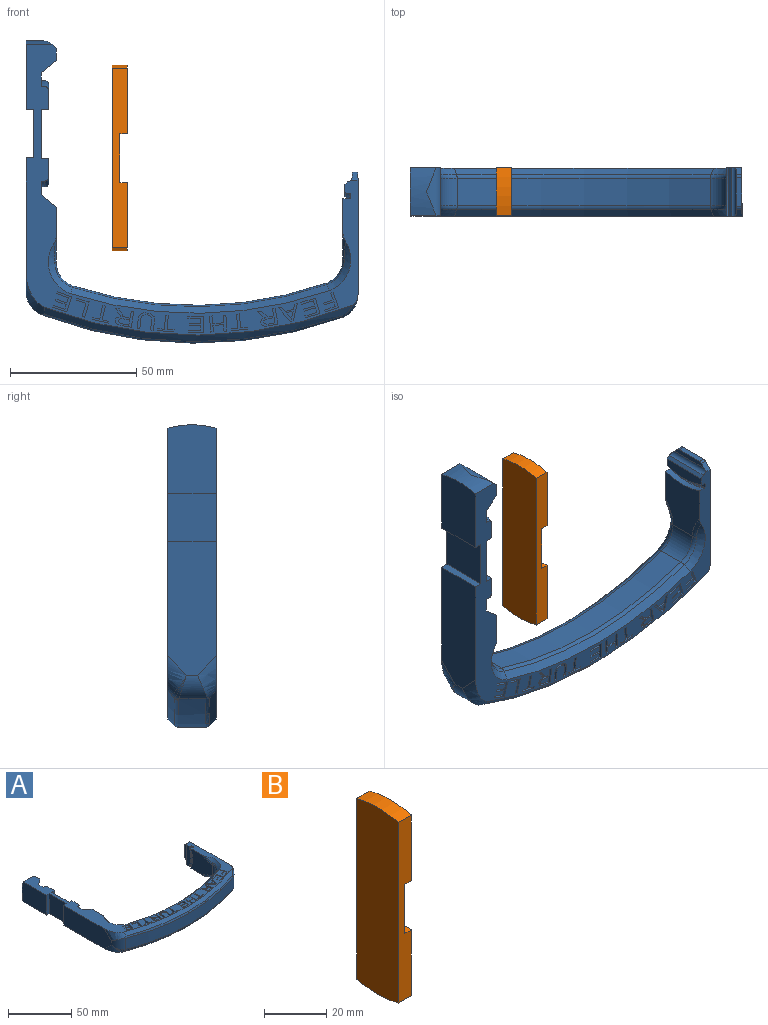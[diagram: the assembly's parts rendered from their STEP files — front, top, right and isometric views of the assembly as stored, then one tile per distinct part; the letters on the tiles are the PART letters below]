
ASSEMBLY  parts=2 mates=1
PART A: 330 faces, bbox 134.4x136.2x59.5 mm
  f0: plane 19.05x1.14mm, normal (-0.71,0.71,0), area 30.8mm2, adj f1,f5,f16,f272
  f1: plane 19.05x4.75mm, normal (-1,0,0), area 78.6mm2, adj f0,f7,f16,f272
  f2: torus R=25.78mm, axis (-1,0,0), area 11.7mm2, adj f3,f6,f16,f272
  f3: plane 19.05x3.09mm, normal (-1,0,0), area 24.8mm2, adj f2,f4,f16,f272
  f4: torus R=27.05mm, axis (-1,0,0), area 11.7mm2, adj f3,f8,f16,f272
  f5: plane 19.05x0.01mm, normal (0,1,0), area 0.1mm2, adj f0,f13,f16,f272
  f6: cylinder r=25.4mm len=19.05mm, axis (1,0,0), area 26.3mm2, adj f2,f7,f16,f272
  f7: cone r=25.15mm half-angle=45deg, axis (1,0,0), area 14mm2, adj f1,f6,f16,f272
  f8: cylinder r=27.43mm len=19.05mm, axis (1,0,0), area 51mm2, adj f4,f16,f18,f272
  f9: plane 2.81x2.81mm, normal (0,0.71,0.71), area 9mm2, adj f10,f12,f13,f16,f17
  f10: cylinder r=1.52mm len=2.29mm, axis (-1,0,0), area 2.7mm2, adj f9,f11,f12,f17
  f11: plane 11.44x2.29mm, normal (0,1,0), area 26.1mm2, adj f10,f12,f15,f17
  f12: plane 16.71x2.01mm, normal (-1,0,0), area 29.4mm2, adj f9,f10,f11,f13,f14,f15
  f13: cylinder r=1.8mm len=19.05mm, axis (0,0,1), area 52.5mm2, adj f5,f9,f12,f14,f16,f272
  f14: plane 2.81x2.81mm, normal (0,0.71,-0.71), area 9mm2, adj f12,f13,f15,f17,f272
  f15: cylinder r=1.52mm len=2.29mm, axis (1,0,0), area 2.7mm2, adj f11,f12,f14,f17
  f16: plane 133.92x117.71mm, normal (0,0,1), area 1900.7mm2, adj f0,f1,f2,f3,f4,f5,f6,f7
  f17: plane 48.39x19.05mm, normal (1,0,0), area 911.7mm2, adj f9,f10,f11,f14,f15,f16,f272,f284
  f18: plane 24.1x19.05mm, normal (-1,0,0), area 379.2mm2, adj f8,f16,f272,f277,f308,f315
  f19: plane 6.1x1.77mm, normal (-0.96,0.28,0), area 9.7mm2, adj f16,f20,f24,f25
  f20: plane 4.95x1.52mm, normal (-0.28,-0.96,0), area 7.9mm2, adj f16,f19,f21,f25
  f21: plane 1.52x0.72mm, normal (0.96,-0.28,0), area 1.1mm2, adj f16,f20,f22,f25
  f22: plane 3.9x1.52mm, normal (0.28,0.96,0), area 6.2mm2, adj f16,f21,f23,f25
  f23: plane 5.38x1.55mm, normal (0.96,-0.28,0), area 8.5mm2, adj f16,f22,f24,f25
  f24: plane 1.52x1.05mm, normal (0.28,0.96,0), area 1.7mm2, adj f16,f19,f23,f25
  f25: plane 7.53x5.16mm, normal (0,0,1), area 10mm2, adj f19,f20,f21,f22,f23,f24
  f26: plane 6.26x1.52mm, normal (-0.99,0.17,0), area 9.7mm2, adj f16,f27,f39,f73
  f27: plane 1.52x1.07mm, normal (-0.18,-0.98,0), area 1.7mm2, adj f16,f26,f28,f73
  f28: plane 2.78x1.52mm, normal (0.98,-0.17,0), area 4.3mm2, adj f16,f27,f29,f73
  f29: plane 1.52x1.25mm, normal (-0.17,-0.99,0), area 1.9mm2, adj f16,f28,f58,f73
  f30: plane 1.52x0.69mm, normal (-0.01,-1,0), area 1.1mm2, adj f16,f31,f72,f73
  f31: plane 1.52x0.64mm, normal (0.14,-0.99,0), area 1mm2, adj f16,f30,f32,f73
  f32: plane 1.52x0.5mm, normal (0.36,-0.93,0), area 0.8mm2, adj f16,f31,f52,f73
  f33: plane 2.07x1.52mm, normal (0.99,-0.17,0), area 3.2mm2, adj f34,f51,f73,f290
  f34: plane 2.57x1.52mm, normal (-0.17,-0.98,0), area 4mm2, adj f33,f40,f73,f290
  f35: plane 1.52x0.5mm, normal (0.58,0.81,0), area 0.9mm2, adj f16,f36,f57,f73
  f36: plane 1.52x0.24mm, normal (0.41,0.91,0), area 0.4mm2, adj f16,f35,f37,f73
  f37: plane 1.52x0.6mm, normal (0.29,0.96,0), area 1mm2, adj f16,f36,f38,f73
  f38: plane 1.52x0.78mm, normal (0.21,0.98,0), area 1.2mm2, adj f16,f37,f39,f73
  f39: plane 3.61x1.52mm, normal (0.17,0.98,0), area 5.6mm2, adj f16,f26,f38,f73
  f40: plane 1.52x0.12mm, normal (-0.14,-0.99,0), area 0.2mm2, adj f34,f41,f73,f290
  f41: plane 1.52x0.69mm, normal (-0.29,-0.96,0), area 1.1mm2, adj f40,f42,f73,f290
  f42: plane 1.52x0.47mm, normal (-0.53,-0.85,0), area 0.8mm2, adj f41,f43,f73,f290
  f43: plane 1.52x0.28mm, normal (-0.79,-0.61,0), area 0.5mm2, adj f42,f44,f73,f290
  f44: plane 1.52x0.52mm, normal (-0.99,-0.13,0), area 0.8mm2, adj f43,f45,f73,f290
  f45: plane 1.52x0.08mm, normal (-0.98,0.22,0), area 0.1mm2, adj f44,f46,f73,f290
  f46: plane 1.52x0.44mm, normal (-0.83,0.55,0), area 0.8mm2, adj f45,f47,f73,f290
  f47: plane 1.52x0.11mm, normal (-0.57,0.82,0), area 0.2mm2, adj f46,f48,f73,f290
  f48: plane 1.52x0.59mm, normal (-0.3,0.96,0), area 0.9mm2, adj f47,f49,f73,f290
  f49: plane 1.52x0.43mm, normal (-0.02,1,0), area 0.7mm2, adj f48,f50,f73,f290
  f50: plane 1.52x0.74mm, normal (0.11,0.99,0), area 1.1mm2, adj f49,f51,f73,f290
  f51: plane 2.31x1.52mm, normal (0.17,0.98,0), area 3.6mm2, adj f33,f50,f73,f290
  f52: plane 1.52x0.22mm, normal (0.52,-0.85,0), area 0.4mm2, adj f16,f32,f53,f73
  f53: plane 1.52x0.39mm, normal (0.74,-0.68,0), area 0.8mm2, adj f16,f52,f54,f73
  f54: plane 1.52x0.49mm, normal (0.94,-0.35,0), area 0.8mm2, adj f16,f53,f55,f73
  f55: plane 1.52x0.49mm, normal (1,0,0), area 0.8mm2, adj f16,f54,f56,f73
  f56: plane 1.52x0.51mm, normal (0.95,0.33,0), area 0.8mm2, adj f16,f55,f57,f73
  f57: plane 1.52x0.39mm, normal (0.8,0.6,0), area 0.7mm2, adj f16,f35,f56,f73
  f58: plane 1.52x0.59mm, normal (-0.22,-0.98,0), area 0.9mm2, adj f16,f29,f59,f73
  f59: plane 1.52x0.46mm, normal (-0.48,-0.88,0), area 0.8mm2, adj f16,f58,f60,f73
  f60: plane 1.52x0.06mm, normal (-0.65,-0.76,0), area 0.1mm2, adj f16,f59,f61,f73
  f61: plane 1.52x0.47mm, normal (-0.75,-0.66,0), area 0.9mm2, adj f16,f60,f62,f73
  f62: plane 1.52x0.01mm, normal (-0.71,-0.71,0), area 0mm2, adj f16,f61,f63,f73
  f63: plane 1.52x0.42mm, normal (-0.83,-0.55,0), area 0.8mm2, adj f16,f62,f64,f73
  f64: plane 1.52x0.57mm, normal (-0.86,-0.52,0), area 1mm2, adj f16,f63,f65,f73
  f65: plane 1.52x1.49mm, normal (-0.87,-0.49,0), area 2.6mm2, adj f16,f64,f66,f73
  f66: plane 1.52x1.36mm, normal (-0.17,-0.99,0), area 2.1mm2, adj f16,f65,f67,f73
  f67: plane 1.95x1.52mm, normal (0.87,0.5,0), area 3.4mm2, adj f16,f66,f68,f73
  f68: plane 1.52x0.05mm, normal (0.83,0.55,0), area 0.1mm2, adj f16,f67,f69,f73
  f69: plane 1.52x0.5mm, normal (0.83,0.56,0), area 0.9mm2, adj f16,f68,f70,f73
  f70: plane 1.52x0.44mm, normal (0.76,0.65,0), area 0.9mm2, adj f16,f69,f71,f73
  f71: plane 1.52x0.05mm, normal (0.71,0.71,0), area 0.1mm2, adj f16,f70,f72,f73
  f72: plane 1.52x0.54mm, normal (0.57,0.82,0), area 1mm2, adj f16,f30,f71,f73
  f73: plane 7.51x7.29mm, normal (0,0,1), area 19.9mm2, adj f26,f27,f28,f29,f30,f31,f32,f33
  f74: plane 3.65x1.52mm, normal (-0.99,0.12,0), area 5.6mm2, adj f16,f75,f89,f113
  f75: plane 1.52x0.06mm, normal (-0.99,0.14,0), area 0.1mm2, adj f16,f74,f76,f113
  f76: plane 1.52x0.6mm, normal (-1,0.06,0), area 0.9mm2, adj f16,f75,f77,f113
  f77: plane 1.52x0.52mm, normal (-1,-0.1,0), area 0.8mm2, adj f16,f76,f78,f113
  f78: plane 1.52x0.44mm, normal (-0.97,-0.26,0), area 0.7mm2, adj f16,f77,f79,f113
  f79: plane 1.52x0.19mm, normal (-0.92,-0.4,0), area 0.3mm2, adj f16,f78,f80,f113
  f80: plane 1.52x0.45mm, normal (-0.79,-0.61,0), area 0.9mm2, adj f16,f79,f98,f113
  f81: plane 1.52x0.59mm, normal (0.18,0.98,0), area 0.9mm2, adj f16,f82,f97,f113
  f82: plane 1.52x0.57mm, normal (0.39,0.92,0), area 0.9mm2, adj f16,f81,f83,f113
  f83: plane 1.52x0.3mm, normal (0.59,0.81,0), area 0.6mm2, adj f16,f82,f84,f113
  f84: plane 1.52x0.47mm, normal (0.83,0.55,0), area 0.9mm2, adj f16,f83,f85,f113
  f85: plane 1.52x0.13mm, normal (0.95,0.3,0), area 0.2mm2, adj f16,f84,f86,f113
  f86: plane 1.52x0.48mm, normal (0.99,0.1,0), area 0.7mm2, adj f16,f85,f87,f113
  f87: plane 1.52x0.62mm, normal (1,-0.07,0), area 0.9mm2, adj f16,f86,f88,f113
  f88: plane 3.64x1.52mm, normal (0.99,-0.12,0), area 5.6mm2, adj f16,f87,f89,f113
  f89: plane 1.52x1.09mm, normal (0.12,0.99,0), area 1.7mm2, adj f16,f74,f88,f113
  f90: plane 3.64x1.52mm, normal (-0.99,0.12,0), area 5.6mm2, adj f16,f91,f112,f113
  f91: plane 1.52x0.21mm, normal (-0.99,0.16,0), area 0.3mm2, adj f16,f90,f92,f113
  f92: plane 1.52x0.59mm, normal (-0.97,0.25,0), area 0.9mm2, adj f16,f91,f93,f113
  f93: plane 1.52x0.44mm, normal (-0.9,0.44,0), area 0.8mm2, adj f16,f92,f94,f113
  f94: plane 1.52x0.3mm, normal (-0.7,0.72,0), area 0.6mm2, adj f16,f93,f95,f113
  f95: plane 1.52x0.37mm, normal (-0.4,0.92,0), area 0.6mm2, adj f16,f94,f96,f113
  f96: plane 1.52x0.61mm, normal (-0.15,0.99,0), area 0.9mm2, adj f16,f95,f97,f113
  f97: plane 1.52x0.78mm, normal (0.05,1,0), area 1.2mm2, adj f16,f81,f96,f113
  f98: plane 1.52x0.5mm, normal (-0.59,-0.81,0), area 0.9mm2, adj f16,f80,f99,f113
  f99: plane 1.52x0.47mm, normal (-0.42,-0.91,0), area 0.8mm2, adj f16,f98,f100,f113
  f100: plane 1.52x0.64mm, normal (-0.29,-0.96,0), area 1mm2, adj f16,f99,f101,f113
  f101: plane 1.52x0.74mm, normal (-0.17,-0.99,0), area 1.1mm2, adj f16,f100,f102,f113
  f102: plane 1.52x0.74mm, normal (-0.07,-1,0), area 1.1mm2, adj f16,f101,f103,f113
  f103: plane 1.52x0.66mm, normal (0.06,-1,0), area 1mm2, adj f16,f102,f104,f113
  f104: plane 1.52x0.57mm, normal (0.23,-0.97,0), area 0.9mm2, adj f16,f103,f105,f113
  f105: plane 1.52x0.23mm, normal (0.35,-0.94,0), area 0.4mm2, adj f16,f104,f106,f113
  f106: plane 1.52x0.52mm, normal (0.5,-0.86,0), area 0.9mm2, adj f16,f105,f107,f113
  f107: plane 1.52x0.4mm, normal (0.74,-0.68,0), area 0.8mm2, adj f16,f106,f108,f113
  f108: plane 1.52x0.38mm, normal (0.88,-0.47,0), area 0.7mm2, adj f16,f107,f109,f113
  f109: plane 1.52x0.5mm, normal (0.95,-0.3,0), area 0.8mm2, adj f16,f108,f110,f113
  f110: plane 1.52x0.59mm, normal (0.99,-0.17,0), area 0.9mm2, adj f16,f109,f111,f113
  f111: plane 3.64x1.52mm, normal (0.99,-0.12,0), area 5.6mm2, adj f16,f110,f112,f113
  f112: plane 1.52x1.09mm, normal (0.12,0.99,0), area 1.7mm2, adj f16,f90,f111,f113
  f113: plane 6.93x6.86mm, normal (0,0,1), area 15.8mm2, adj f74,f75,f76,f77,f78,f79,f80,f81
  f114: plane 6.35x1.52mm, normal (-1,0,0), area 9.7mm2, adj f16,f115,f125,f126
  f115: plane 6.16x1.52mm, normal (0,-1,0), area 9.4mm2, adj f16,f114,f116,f126
  f116: plane 1.52x0.75mm, normal (1,0,0), area 1.1mm2, adj f16,f115,f117,f126
  f117: plane 5.06x1.52mm, normal (0,1,0), area 7.7mm2, adj f16,f116,f118,f126
  f118: plane 2.17x1.52mm, normal (1,0,0), area 3.3mm2, adj f16,f117,f119,f126
  f119: plane 4.56x1.52mm, normal (0,-1,0), area 6.9mm2, adj f16,f118,f120,f126
  f120: plane 1.52x0.74mm, normal (1,0,0), area 1.1mm2, adj f16,f119,f121,f126
  f121: plane 4.56x1.52mm, normal (0,1,0), area 6.9mm2, adj f16,f120,f122,f126
  f122: plane 1.94x1.52mm, normal (1,0,0), area 3mm2, adj f16,f121,f123,f126
  f123: plane 4.87x1.52mm, normal (0,-1,0), area 7.4mm2, adj f16,f122,f124,f126
  f124: plane 1.52x0.74mm, normal (1,0,0), area 1.1mm2, adj f16,f123,f125,f126
  f125: plane 5.96x1.52mm, normal (0,1,0), area 9.1mm2, adj f16,f114,f124,f126
  f126: plane 6.35x6.16mm, normal (0,0,1), area 17.8mm2, adj f114,f115,f116,f117,f118,f119,f120,f121
  f127: plane 6.34x1.52mm, normal (-1,-0.06,0), area 9.7mm2, adj f16,f128,f132,f139
  f128: plane 1.52x1.09mm, normal (0.05,-1,0), area 1.7mm2, adj f16,f127,f129,f139
  f129: plane 2.99x1.52mm, normal (1,0.06,0), area 4.6mm2, adj f16,f128,f130,f139
  f130: plane 4.28x1.52mm, normal (0.05,-1,0), area 6.5mm2, adj f16,f129,f135,f139
  f131: plane 2.61x1.52mm, normal (1,0.05,0), area 4mm2, adj f16,f132,f134,f139
  f132: plane 1.52x1.1mm, normal (-0.05,1,0), area 1.7mm2, adj f16,f127,f131,f139
  f133: plane 2.61x1.52mm, normal (-1,-0.05,0), area 4mm2, adj f16,f134,f138,f139
  f134: plane 4.27x1.52mm, normal (-0.05,1,0), area 6.5mm2, adj f16,f131,f133,f139
  f135: plane 2.99x1.52mm, normal (-1,-0.06,0), area 4.6mm2, adj f16,f130,f136,f139
  f136: plane 1.52x1.09mm, normal (0.05,-1,0), area 1.7mm2, adj f16,f135,f137,f139
  f137: plane 6.34x1.52mm, normal (1,0.05,0), area 9.7mm2, adj f16,f136,f138,f139
  f138: plane 1.52x1.09mm, normal (-0.05,1,0), area 1.7mm2, adj f16,f133,f137,f139
  f139: plane 6.81x6.69mm, normal (0,0,1), area 17.1mm2, adj f127,f128,f129,f130,f131,f132,f133,f134
  f140: plane 6.25x1.52mm, normal (-0.98,-0.18,0), area 9.7mm2, adj f16,f141,f153,f187
  f141: plane 1.52x1.08mm, normal (0.18,-0.98,0), area 1.7mm2, adj f16,f140,f142,f187
  f142: plane 2.78x1.52mm, normal (0.98,0.18,0), area 4.3mm2, adj f16,f141,f143,f187
  f143: plane 1.52x1.25mm, normal (0.18,-0.98,0), area 1.9mm2, adj f16,f142,f172,f187
  f144: plane 1.52x0.65mm, normal (0.34,-0.94,0), area 1.1mm2, adj f16,f145,f186,f187
  f145: plane 1.52x0.57mm, normal (0.47,-0.88,0), area 1mm2, adj f16,f144,f146,f187
  f146: plane 1.52x0.4mm, normal (0.66,-0.75,0), area 0.8mm2, adj f16,f145,f166,f187
  f147: plane 2.07x1.52mm, normal (0.98,0.18,0), area 3.2mm2, adj f148,f165,f187,f271
  f148: plane 2.57x1.52mm, normal (0.18,-0.98,0), area 4mm2, adj f147,f154,f187,f271
  f149: plane 1.52x0.59mm, normal (0.27,0.96,0), area 0.9mm2, adj f16,f150,f171,f187
  f150: plane 1.52x0.26mm, normal (0.06,1,0), area 0.4mm2, adj f16,f149,f151,f187
  f151: plane 1.52x0.64mm, normal (-0.05,1,0), area 1mm2, adj f16,f150,f152,f187
  f152: plane 1.52x0.79mm, normal (-0.15,0.99,0), area 1.2mm2, adj f16,f151,f153,f187
  f153: plane 3.6x1.52mm, normal (-0.18,0.98,0), area 5.6mm2, adj f16,f140,f152,f187
  f154: plane 1.52x0.11mm, normal (0.15,-0.99,0), area 0.2mm2, adj f148,f155,f187,f271
  f155: plane 1.52x0.73mm, normal (0.07,-1,0), area 1.1mm2, adj f154,f156,f187,f271
  f156: plane 1.52x0.54mm, normal (-0.21,-0.98,0), area 0.8mm2, adj f155,f157,f187,f271
  f157: plane 1.52x0.31mm, normal (-0.54,-0.84,0), area 0.6mm2, adj f156,f158,f187,f271
  f158: plane 1.52x0.45mm, normal (-0.88,-0.47,0), area 0.8mm2, adj f157,f159,f187,f271
  f159: plane 1.52x0.08mm, normal (-1,-0.1,0), area 0.1mm2, adj f158,f160,f187,f271
  f160: plane 1.52x0.52mm, normal (-0.97,0.24,0), area 0.8mm2, adj f159,f161,f187,f271
  f161: plane 1.52x0.11mm, normal (-0.82,0.57,0), area 0.2mm2, adj f160,f162,f187,f271
  f162: plane 1.52x0.49mm, normal (-0.61,0.8,0), area 0.9mm2, adj f161,f163,f187,f271
  f163: plane 1.52x0.39mm, normal (-0.36,0.93,0), area 0.6mm2, adj f162,f164,f187,f271
  f164: plane 1.52x0.74mm, normal (-0.23,0.97,0), area 1.2mm2, adj f163,f165,f187,f271
  f165: plane 2.31x1.52mm, normal (-0.17,0.98,0), area 3.6mm2, adj f147,f164,f187,f271
  f166: plane 1.52x0.21mm, normal (0.81,-0.58,0), area 0.4mm2, adj f16,f146,f167,f187
  f167: plane 1.52x0.49mm, normal (0.92,-0.4,0), area 0.8mm2, adj f16,f166,f168,f187
  f168: plane 1.52x0.53mm, normal (1,0,0), area 0.8mm2, adj f16,f167,f169,f187
  f169: plane 1.52x0.47mm, normal (0.94,0.34,0), area 0.8mm2, adj f16,f168,f170,f187
  f170: plane 1.52x0.42mm, normal (0.78,0.62,0), area 0.8mm2, adj f16,f169,f171,f187
  f171: plane 1.52x0.42mm, normal (0.54,0.84,0), area 0.8mm2, adj f16,f149,f170,f187
  f172: plane 1.52x0.61mm, normal (0.12,-0.99,0), area 0.9mm2, adj f16,f143,f173,f187
  f173: plane 1.52x0.52mm, normal (-0.14,-0.99,0), area 0.8mm2, adj f16,f172,f174,f187
  f174: plane 1.52x0.07mm, normal (-0.35,-0.94,0), area 0.1mm2, adj f16,f173,f175,f187
  f175: plane 1.52x0.55mm, normal (-0.48,-0.88,0), area 1mm2, adj f16,f174,f176,f187
  f176: plane 1.52x0.01mm, normal (0,-1,0), area 0mm2, adj f16,f175,f177,f187
  f177: plane 1.52x0.41mm, normal (-0.59,-0.81,0), area 0.8mm2, adj f16,f176,f178,f187
  f178: plane 1.52x0.51mm, normal (-0.63,-0.77,0), area 1mm2, adj f16,f177,f179,f187
  f179: plane 1.52x1.31mm, normal (-0.65,-0.76,0), area 2.6mm2, adj f16,f178,f180,f187
  f180: plane 1.52x1.36mm, normal (0.18,-0.98,0), area 2.1mm2, adj f16,f179,f181,f187
  f181: plane 1.72x1.52mm, normal (0.65,0.76,0), area 3.4mm2, adj f16,f180,f182,f187
  f182: plane 1.52x0.05mm, normal (0.55,0.83,0), area 0.1mm2, adj f16,f181,f183,f187
  f183: plane 1.52x0.49mm, normal (0.59,0.81,0), area 0.9mm2, adj f16,f182,f184,f187
  f184: plane 1.52x0.5mm, normal (0.48,0.88,0), area 0.9mm2, adj f16,f183,f185,f187
  f185: plane 1.52x0.07mm, normal (0.35,0.94,0), area 0.1mm2, adj f16,f184,f186,f187
  f186: plane 1.52x0.64mm, normal (0.25,0.97,0), area 1mm2, adj f16,f144,f185,f187
  f187: plane 8.27x7.04mm, normal (0,0,1), area 19.9mm2, adj f140,f141,f142,f143,f144,f145,f146,f147
  f188: plane 1.52x0.24mm, normal (-0.82,-0.57,0), area 0.4mm2, adj f189,f203,f205,f270
  f189: plane 1.52x0.42mm, normal (-0.8,-0.61,0), area 0.8mm2, adj f188,f190,f205,f270
  f190: plane 1.52x0.49mm, normal (-0.79,-0.61,0), area 1mm2, adj f189,f191,f205,f270
  f191: plane 1.52x1.51mm, normal (-0.77,-0.63,0), area 3mm2, adj f190,f192,f205,f270
  f192: plane 2.72x1.52mm, normal (-0.23,0.97,0), area 4.3mm2, adj f191,f200,f205,f270
  f193: plane 1.65x1.52mm, normal (-0.77,-0.64,0), area 3.3mm2, adj f16,f194,f199,f205
  f194: plane 1.52x1.2mm, normal (0.23,-0.97,0), area 1.9mm2, adj f16,f193,f195,f205
  f195: plane 5.41x4.73mm, normal (0.75,0.66,0), area 11mm2, adj f16,f194,f204,f205
  f196: plane 6.91x1.64mm, normal (-0.97,0.23,0), area 10.8mm2, adj f16,f197,f204,f205
  f197: plane 1.52x1.13mm, normal (0.23,-0.97,0), area 1.8mm2, adj f16,f196,f198,f205
  f198: plane 2.08x1.52mm, normal (0.98,-0.21,0), area 3.2mm2, adj f16,f197,f199,f205
  f199: plane 3.35x1.52mm, normal (0.23,-0.97,0), area 5.2mm2, adj f16,f193,f198,f205
  f200: plane 2.02x1.52mm, normal (0.97,-0.22,0), area 3.2mm2, adj f192,f201,f205,f270
  f201: plane 1.52x0.22mm, normal (0.98,-0.19,0), area 0.3mm2, adj f200,f202,f205,f270
  f202: plane 1.52x0.54mm, normal (0.99,-0.14,0), area 0.8mm2, adj f201,f203,f205,f270
  f203: plane 1.52x0.54mm, normal (1,-0.06,0), area 0.8mm2, adj f188,f202,f205,f270
  f204: plane 1.52x1.15mm, normal (-0.23,0.97,0), area 1.8mm2, adj f16,f195,f196,f205
  f205: plane 7.51x7.18mm, normal (0,0,1), area 15.7mm2, adj f188,f189,f190,f191,f192,f193,f194,f195
  f206: plane 6.01x2.06mm, normal (-0.95,-0.32,0), area 9.7mm2, adj f16,f207,f215,f216
  f207: plane 1.52x1.04mm, normal (0.33,-0.94,0), area 1.7mm2, adj f16,f206,f208,f216
  f208: plane 2.73x1.52mm, normal (0.95,0.32,0), area 4.4mm2, adj f16,f207,f209,f216
  f209: plane 3.66x1.52mm, normal (0.32,-0.95,0), area 5.9mm2, adj f16,f208,f210,f216
  f210: plane 1.52x0.71mm, normal (0.95,0.32,0), area 1.1mm2, adj f16,f209,f211,f216
  f211: plane 3.66x1.52mm, normal (-0.32,0.95,0), area 5.9mm2, adj f16,f210,f212,f216
  f212: plane 1.86x1.52mm, normal (0.95,0.32,0), area 3mm2, adj f16,f211,f213,f216
  f213: plane 4.23x1.52mm, normal (0.33,-0.95,0), area 6.8mm2, adj f16,f212,f214,f216
  f214: plane 1.52x0.7mm, normal (0.95,0.33,0), area 1.1mm2, adj f16,f213,f215,f216
  f215: plane 5.27x1.81mm, normal (-0.32,0.95,0), area 8.5mm2, adj f16,f206,f214,f216
  f216: plane 7.81x5.82mm, normal (0,0,1), area 13.2mm2, adj f206,f207,f208,f209,f210,f211,f212,f213
  f217: plane 6.1x1.77mm, normal (-0.96,-0.28,0), area 9.7mm2, adj f16,f218,f228,f229
  f218: plane 5.91x1.72mm, normal (0.28,-0.96,0), area 9.4mm2, adj f16,f217,f219,f229
  f219: plane 1.52x0.72mm, normal (0.96,0.28,0), area 1.1mm2, adj f16,f218,f220,f229
  f220: plane 4.86x1.52mm, normal (-0.28,0.96,0), area 7.7mm2, adj f16,f219,f221,f229
  f221: plane 2.07x1.52mm, normal (0.96,0.28,0), area 3.3mm2, adj f16,f220,f222,f229
  f222: plane 4.38x1.52mm, normal (0.28,-0.96,0), area 7mm2, adj f16,f221,f223,f229
  f223: plane 1.52x0.71mm, normal (0.96,0.28,0), area 1.1mm2, adj f16,f222,f224,f229
  f224: plane 4.38x1.52mm, normal (-0.28,0.96,0), area 7mm2, adj f16,f223,f225,f229
  f225: plane 1.87x1.52mm, normal (0.96,0.27,0), area 3mm2, adj f16,f224,f226,f229
  f226: plane 4.68x1.52mm, normal (0.28,-0.96,0), area 7.4mm2, adj f16,f225,f227,f229
  f227: plane 1.52x0.72mm, normal (0.96,0.28,0), area 1.1mm2, adj f16,f226,f228,f229
  f228: plane 5.73x1.66mm, normal (-0.28,0.96,0), area 9.1mm2, adj f16,f217,f227,f229
  f229: plane 7.76x7.68mm, normal (0,0,1), area 17.8mm2, adj f217,f218,f219,f220,f221,f222,f223,f224
  f230: plane 1.52x0.75mm, normal (-1,-0.1,0), area 1.2mm2, adj f16,f231,f237,f238
  f231: plane 2.7x1.52mm, normal (0.1,-0.99,0), area 4.1mm2, adj f16,f230,f232,f238
  f232: plane 5.57x1.52mm, normal (-0.99,-0.1,0), area 8.5mm2, adj f16,f231,f233,f238
  f233: plane 1.52x1.09mm, normal (0.11,-0.99,0), area 1.7mm2, adj f16,f232,f234,f238
  f234: plane 5.57x1.52mm, normal (0.99,0.1,0), area 8.5mm2, adj f16,f233,f235,f238
  f235: plane 2.72x1.52mm, normal (0.1,-0.99,0), area 4.2mm2, adj f16,f234,f236,f238
  f236: plane 1.52x0.74mm, normal (0.99,0.11,0), area 1.1mm2, adj f16,f235,f237,f238
  f237: plane 6.5x1.52mm, normal (-0.1,0.99,0), area 10mm2, adj f16,f230,f236,f238
  f238: plane 6.72x6.58mm, normal (0,0,1), area 11mm2, adj f230,f231,f232,f233,f234,f235,f236,f237
  f239: plane 1.52x0.74mm, normal (-1,0.07,0), area 1.1mm2, adj f16,f240,f246,f247
  f240: plane 2.71x1.52mm, normal (-0.07,-1,0), area 4.1mm2, adj f16,f239,f241,f247
  f241: plane 5.58x1.52mm, normal (-1,0.07,0), area 8.5mm2, adj f16,f240,f242,f247
  f242: plane 1.52x1.09mm, normal (-0.08,-1,0), area 1.7mm2, adj f16,f241,f243,f247
  f243: plane 5.59x1.52mm, normal (1,-0.07,0), area 8.5mm2, adj f16,f242,f244,f247
  f244: plane 2.72x1.52mm, normal (-0.07,-1,0), area 4.2mm2, adj f16,f243,f245,f247
  f245: plane 1.52x0.74mm, normal (1,-0.08,0), area 1.1mm2, adj f16,f244,f246,f247
  f246: plane 6.53x1.52mm, normal (0.07,1,0), area 10mm2, adj f16,f239,f245,f247
  f247: plane 6.61x6.58mm, normal (0,0,1), area 11mm2, adj f239,f240,f241,f242,f243,f244,f245,f246
  f248: plane 1.52x0.73mm, normal (-0.97,0.23,0), area 1.1mm2, adj f16,f249,f255,f256
  f249: plane 2.65x1.52mm, normal (-0.23,-0.97,0), area 4.1mm2, adj f16,f248,f250,f256
  f250: plane 5.45x1.52mm, normal (-0.97,0.23,0), area 8.5mm2, adj f16,f249,f251,f256
  f251: plane 1.52x1.06mm, normal (-0.23,-0.97,0), area 1.7mm2, adj f16,f250,f252,f256
  f252: plane 5.45x1.52mm, normal (0.97,-0.23,0), area 8.5mm2, adj f16,f251,f253,f256
  f253: plane 2.66x1.52mm, normal (-0.22,-0.97,0), area 4.2mm2, adj f16,f252,f254,f256
  f254: plane 1.52x0.73mm, normal (0.97,-0.22,0), area 1.1mm2, adj f16,f253,f255,f256
  f255: plane 6.37x1.52mm, normal (0.23,0.97,0), area 10mm2, adj f16,f248,f254,f256
  f256: plane 7.05x6.54mm, normal (0,0,1), area 11mm2, adj f248,f249,f250,f251,f252,f253,f254,f255
  f257: plane 6.01x2.05mm, normal (-0.95,0.32,0), area 9.7mm2, adj f16,f258,f268,f269
  f258: plane 5.82x1.99mm, normal (-0.32,-0.95,0), area 9.4mm2, adj f16,f257,f259,f269
  f259: plane 1.52x0.71mm, normal (0.95,-0.32,0), area 1.1mm2, adj f16,f258,f260,f269
  f260: plane 4.79x1.64mm, normal (0.32,0.95,0), area 7.7mm2, adj f16,f259,f261,f269
  f261: plane 2.04x1.52mm, normal (0.95,-0.33,0), area 3.3mm2, adj f16,f260,f262,f269
  f262: plane 4.32x1.52mm, normal (-0.32,-0.95,0), area 7mm2, adj f16,f261,f263,f269
  f263: plane 1.52x0.7mm, normal (0.95,-0.33,0), area 1.1mm2, adj f16,f262,f264,f269
  f264: plane 4.32x1.52mm, normal (0.32,0.95,0), area 7mm2, adj f16,f263,f265,f269
  f265: plane 1.84x1.52mm, normal (0.95,-0.32,0), area 3mm2, adj f16,f264,f266,f269
  f266: plane 4.61x1.58mm, normal (-0.32,-0.95,0), area 7.4mm2, adj f16,f265,f267,f269
  f267: plane 1.52x0.71mm, normal (0.95,-0.32,0), area 1.1mm2, adj f16,f266,f268,f269
  f268: plane 5.65x1.93mm, normal (0.32,0.95,0), area 9.1mm2, adj f16,f257,f267,f269
  f269: plane 8.01x7.7mm, normal (0,0,1), area 17.8mm2, adj f257,f258,f259,f260,f261,f262,f263,f264
  f270: plane 3.3x2.72mm, normal (0,0,1), area 4.1mm2, adj f188,f189,f190,f191,f192,f200,f201,f202
  f271: plane 4.5x2.59mm, normal (0,0,1), area 8.4mm2, adj f147,f148,f154,f155,f156,f157,f158,f159
  f272: plane 132.03x115.82mm, normal (0,0,-1), area 2119.6mm2, adj f0,f1,f2,f3,f4,f5,f6,f7
  f273: torus R=12.29mm, axis (0,0,1), area 22.2mm2, adj f274,f277,f279,f315
  f274: torus R=159.79mm, axis (0,0,1), area 184mm2, adj f273,f275,f278,f316
  f275: torus R=12.29mm, axis (0,0,1), area 22.6mm2, adj f274,f276,f280,f317
  f276: bspline ~10.88x5.74mm, area 19.3mm2, adj f272,f275,f280,f318
  f277: bspline ~10.88x5.74mm, area 19.2mm2, adj f18,f272,f273,f279
  f278: cone r=159.09mm half-angle=45deg, axis (0,0,-1), area 367.2mm2, adj f272,f274,f279,f280
  f279: cone r=11.59mm half-angle=45deg, axis (0,0,-1), area 64mm2, adj f272,f273,f277,f278
  f280: cone r=11.59mm half-angle=45deg, axis (0,0,-1), area 64.9mm2, adj f272,f275,f276,f278
  f281: torus R=168.99mm, axis (0,0,-1), area 215.2mm2, adj f282,f283,f285,f326
  f282: bspline ~8.14x6.6mm, area 19.7mm2, adj f272,f281,f283,f284
  f283: cone r=169.69mm half-angle=45deg, axis (0,0,1), area 432.3mm2, adj f272,f281,f282,f328,f329
  f284: cylinder r=10mm len=19.05mm, axis (0,0,1), area 171.3mm2, adj f16,f17,f272,f282,f285,f313
  f285: cylinder r=171.28mm len=118.83mm, axis (0,0,1), area 1311.3mm2, adj f281,f284,f312,f324,f326
  f286: plane 19.05x19.05mm, normal (-1,0,0), area 362.9mm2, adj f16,f272,f319,f321
  f287: cylinder r=36.87mm len=19.05mm, axis (-1,0,0), area 161.7mm2, adj f16,f272,f288,f322
  f288: cylinder r=6.35mm len=19.05mm, axis (0,0,-1), area 88.1mm2, adj f16,f272,f287,f289
  f289: plane 19.05x4.52mm, normal (1,0,0), area 66.7mm2, adj f16,f272,f288,f299
  f290: plane 4.49x2.56mm, normal (0,0,1), area 8.4mm2, adj f33,f34,f40,f41,f42,f43,f44,f45
  f291: plane 19.05x3.02mm, normal (0,-1,0), area 57.6mm2, adj f16,f272,f293,f303
  f292: plane 19.05x3.02mm, normal (0,1,0), area 57.6mm2, adj f16,f272,f293,f294
  f293: plane 19.56x19.05mm, normal (1,0,0), area 372.6mm2, adj f16,f272,f291,f292
  f294: plane 19.05x9.7mm, normal (1,0,0), area 169.4mm2, adj f16,f272,f292,f298
  f295: cone r=28.37mm half-angle=37.8deg, axis (1,0,0), area 148.3mm2, adj f16,f272,f296,f318
  f296: plane 19.05x7.33mm, normal (1,0,0), area 98.9mm2, adj f16,f272,f295,f297
  f297: cylinder r=21mm len=19.05mm, axis (-1,0,0), area 29.2mm2, adj f16,f272,f296,f298
  f298: torus R=19.48mm, axis (1,0,0), area 48mm2, adj f16,f272,f294,f297
  f299: cone r=28.37mm half-angle=37.8deg, axis (1,0,0), area 148.3mm2, adj f16,f272,f289,f300
  f300: plane 19.05x7.33mm, normal (1,0,0), area 98.9mm2, adj f16,f272,f299,f301
  f301: cylinder r=21mm len=19.05mm, axis (1,0,0), area 29.2mm2, adj f16,f272,f300,f302
  f302: torus R=19.48mm, axis (1,0,0), area 48mm2, adj f16,f272,f301,f303
  f303: plane 19.05x9.7mm, normal (1,0,0), area 169.4mm2, adj f16,f272,f291,f302
  f304: torus R=12.29mm, axis (0,0,-1), area 22.2mm2, adj f305,f308,f310,f315
  f305: torus R=159.79mm, axis (0,0,-1), area 184mm2, adj f304,f306,f309,f316
  f306: torus R=12.29mm, axis (0,0,-1), area 22.6mm2, adj f305,f307,f311,f317
  f307: bspline ~10.88x5.74mm, area 19.3mm2, adj f16,f306,f311,f318
  f308: bspline ~10.88x5.74mm, area 19.2mm2, adj f16,f18,f304,f310
  f309: cone r=159.09mm half-angle=45deg, axis (0,0,1), area 367.2mm2, adj f16,f305,f310,f311
  f310: cone r=11.59mm half-angle=45deg, axis (0,0,1), area 63.9mm2, adj f16,f304,f308,f309
  f311: cone r=11.59mm half-angle=45deg, axis (0,0,1), area 65.1mm2, adj f16,f306,f307,f309
  f312: torus R=168.99mm, axis (0,0,1), area 218.3mm2, adj f285,f313,f314,f323,f324
  f313: bspline ~8.14x6.6mm, area 19.7mm2, adj f16,f284,f312,f314
  f314: cone r=169.69mm half-angle=45deg, axis (0,0,-1), area 433.7mm2, adj f16,f312,f313,f323
  f315: cylinder r=10mm len=10.81mm, axis (0,0,1), area 130.4mm2, adj f18,f273,f304,f316
  f316: cylinder r=157.51mm len=100.55mm, axis (0,0,1), area 1106mm2, adj f274,f305,f315,f317
  f317: cylinder r=10mm len=10.81mm, axis (0,0,1), area 133.2mm2, adj f275,f306,f316,f318
  f318: plane 21.74x19.05mm, normal (1,0,0), area 336.8mm2, adj f16,f272,f276,f295,f307,f317
  f319: plane 19.05x3mm, normal (0,1,0), area 57.1mm2, adj f16,f272,f286,f320
  f320: plane 52.95x19.05mm, normal (-1,0,0), area 951.3mm2, adj f16,f272,f319,f323,f324,f329
  f321: plane 19.05x3mm, normal (0,-1,0), area 57.1mm2, adj f16,f272,f286,f322
  f322: plane 27.35x19.05mm, normal (-1,0,0), area 513.1mm2, adj f16,f272,f287,f321
  f323: bspline ~37.61x35.85mm, area 102.4mm2, adj f16,f312,f314,f320,f324
  f324: cylinder r=10mm len=11.31mm, axis (0,0,1), area 99mm2, adj f285,f312,f320,f323,f325,f327
  f325: bspline ~7.3x5.82mm, area 9.4mm2, adj f324,f326,f327,f328
  f326: bspline ~2.66x1.83mm, area 2.5mm2, adj f281,f285,f325,f328
  f327: bspline ~5.52x2.77mm, area 1.4mm2, adj f324,f325,f329
  f328: bspline ~10.63x8.72mm, area 10.2mm2, adj f283,f325,f326,f329
  f329: bspline ~50.27x47.76mm, area 77.6mm2, adj f272,f283,f320,f327,f328
PART B: 10 faces, bbox 6x18.9x73.7 mm
  f0: plane 19.4x18.9mm, normal (1,0,0), area 366.7mm2, adj f1,f3,f7,f9
  f1: plane 71.28x5.98mm, normal (0,-1,0), area 368.2mm2, adj f0,f2,f4,f5,f6,f7,f8,f9
  f2: cylinder r=36.87mm len=18.9mm, axis (1,0,0), area 114.2mm2, adj f1,f3,f5,f8
  f3: plane 71.28x5.98mm, normal (0,1,0), area 368.2mm2, adj f0,f2,f4,f5,f6,f7,f8,f9
  f4: cylinder r=36.87mm len=18.9mm, axis (1,0,0), area 114.2mm2, adj f1,f3,f5,f6
  f5: plane 73.75x18.9mm, normal (-1,0,0), area 1378.4mm2, adj f1,f2,f3,f4
  f6: plane 27.17x18.9mm, normal (1,0,0), area 505.9mm2, adj f1,f3,f4,f7
  f7: plane 18.9x2.98mm, normal (0,0,1), area 56.2mm2, adj f0,f1,f3,f6
  f8: plane 27.17x18.9mm, normal (1,0,0), area 505.9mm2, adj f1,f2,f3,f9
  f9: plane 18.9x2.98mm, normal (0,0,-1), area 56.2mm2, adj f0,f1,f3,f8
PLACE A rot(axis=(1,0,0),90deg) t=(-34.25,-26.17,54.76)mm
PLACE B at identity fixed
MATE fastened A.f272 <-> B.f3  axis (0,1,0) through (-25.25,-26.17,-15.48)mm
